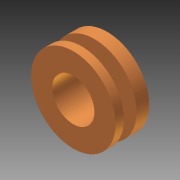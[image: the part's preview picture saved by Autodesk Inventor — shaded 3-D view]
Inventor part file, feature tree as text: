
AUTODESK INVENTOR PART (.ipt)
format: ipt  version: 2011 (Build 150239000, 239)  size: 98,816 bytes
history: native  units: in
note: dims shown in document units (in); Inventor stores cm internally (conversion verified against a paired STEP export)
features: extrude x4, sketch x4, projected_geometry x1
ambient origin geometry x8: Origin, YZ Plane, XZ Plane, XY Plane, X Axis, Y Axis, Z Axis, Center Point
bodies: Solid1 (feature_tree)
feature tree (9):
  extrude  "Extrusion1"  Depth=0.075in TaperAngle=0.0deg
  extrude  "Extrusion2"  Depth=0.075in TaperAngle=0.0deg
  extrude  "Extrusion3"  Depth=0.25in
  extrude  "Extrusion4"  [1 undecoded]
  sketch  "Sketch1"  dims[d0=0.5in d1=0.075in d2=0.0in]
  sketch  "Sketch2"  dims[d3=0.275in d4=0.075in d5=0.0in]
  sketch  "Sketch3"  dims[d6=0.05in d7=0.0in d8=0.25in]
  projected_geometry  "Projected Loop1"
  sketch  "Sketch4"  dims[d9=0.05in d10=0.0in]
note: 1 required parameter value undecoded (feature->parameter linkage not recoverable at this tier; creation-order binding heuristic only, values carry confidence <= 0.55)
